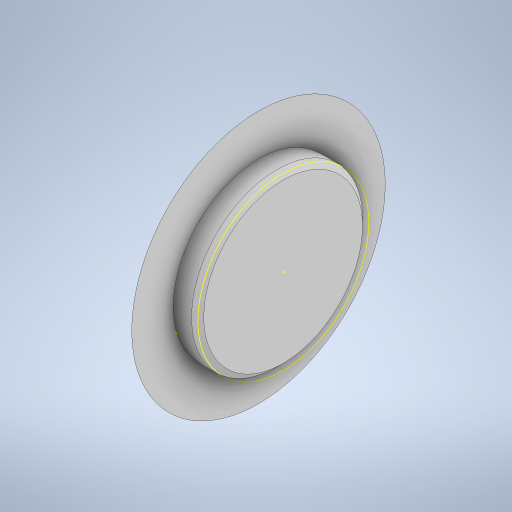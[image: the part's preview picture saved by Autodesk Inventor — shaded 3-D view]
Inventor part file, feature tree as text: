
AUTODESK INVENTOR PART (.ipt)
format: ipt  version: 2024.2 (Build 282272000, 272)  size: 315,904 bytes
history: native  units: in
note: dims shown in document units (in); Inventor stores cm internally (conversion verified against a paired STEP export)
features: sketch x2, revolve x1, chamfer x1
ambient origin geometry x8: Origin, YZ Plane, XZ Plane, XY Plane, X Axis, Y Axis, Z Axis, Center Point
bodies: Body1 (feature_tree)
feature tree (4):
  revolve  "Revolution3"  [1 undecoded]
  chamfer  "Chamfer2"  Distance=0.5118in
  sketch  "Sketch2"  dims[d34=0.5512in d35=0.5118in d36=0.1575in d37=90.0deg d38=0.0394in d39=0.0787in d40=45.0deg]
  sketch  "Sketch1"  dims[d20=0.3937in d21=0.0394in d22=0.9843in d23=0.0787in d24=0.659in d25=1.2044in d26=0.4362in d27=1.6142in d28=0.4362in d33=1.3386in]
note: 1 required parameter value undecoded (feature->parameter linkage not recoverable at this tier; creation-order binding heuristic only, values carry confidence <= 0.55)
